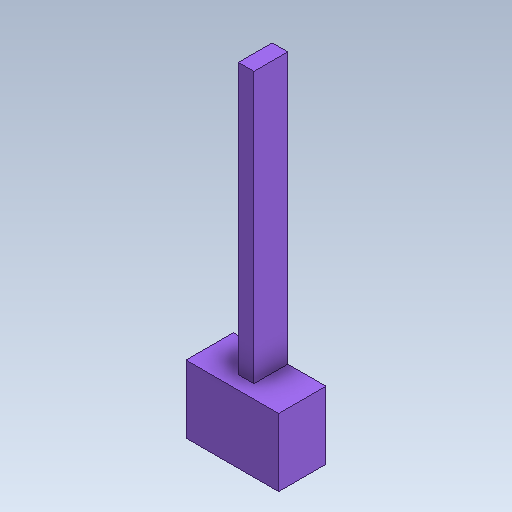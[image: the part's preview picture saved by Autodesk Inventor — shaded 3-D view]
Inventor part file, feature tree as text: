
AUTODESK INVENTOR PART (.ipt)
format: ipt  version: 2020 (Build 240168000, 168)  size: 260,608 bytes
history: native  units: in
note: dims shown in document units (in); Inventor stores cm internally (conversion verified against a paired STEP export)
features: extrude x13, sketch x13, projected_geometry x12
ambient origin geometry x8: Origin, YZ Plane, XZ Plane, XY Plane, X Axis, Y Axis, Z Axis, Center Point
bodies: Solid1 (feature_tree)
feature tree (38):
  extrude  "Extrusion1"  Depth=0.7874in
  extrude  "Extrusion4"  Depth=0.2894in
  extrude  "Extrusion5"  Depth=0.1378in TaperAngle=0.0deg
  extrude  "Extrusion6"  Depth=0.0797in
  extrude  "Extrusion7"  Depth=0.1575in
  extrude  "Extrusion8"  Depth=0.0787in TaperAngle=0.0deg
  extrude  "Extrusion9"  Depth=0.0394in
  extrude  "Extrusion10"  Depth=0.0689in TaperAngle=0.0deg
  extrude  "Extrusion11"  Depth=0.3937in TaperAngle=0.0deg
  extrude  "Extrusion12"  Depth=0.3937in TaperAngle=0.0deg
  extrude  "Extrusion17"  Depth=0.3937in TaperAngle=0.0deg
  extrude  "Extrusion18"  Depth=0.0039in
  extrude  "Extrusion19"  Depth=0.0394in TaperAngle=0.0deg
  sketch  "Sketch1"  dims[d0=0.7874in d1=0.1358in]
  sketch  "Sketch4"  dims[d2=0.1457in d3=0.2894in]
  projected_geometry  "Projected Loop3"
  sketch  "Sketch5"  dims[d4=0.1969in d5=0.1378in d6=0.0in]
  projected_geometry  "Projected Loop4"
  sketch  "Sketch6"  dims[d22=0.0797in d23=0.0797in]
  projected_geometry  "Projected Loop5"
  sketch  "Sketch7"  dims[d24=0.2953in d25=0.1575in]
  projected_geometry  "Projected Loop6"
  sketch  "Sketch8"  dims[d26=0.122in d27=0.0787in d28=0.0in]
  projected_geometry  "Projected Loop7"
  sketch  "Sketch9"  dims[d29=0.0394in d30=0.0394in]
  projected_geometry  "Projected Loop8"
  sketch  "Sketch10"  dims[d31=0.3937in d32=0.0in d33=0.0689in d34=0.0in]
  projected_geometry  "Projected Loop9"
  sketch  "Sketch11"  dims[d35=0.0197in d36=0.3937in d37=0.0in]
  projected_geometry  "Projected Loop10"
  sketch  "Sketch12"  dims[d38=0.0787in d39=0.0in d40=0.3937in d41=0.0in]
  projected_geometry  "Projected Loop11"
  sketch  "Sketch17"  dims[d42=0.3937in d43=0.0in d44=0.3937in d45=0.0in]
  projected_geometry  "Projected Loop16"
  sketch  "Sketch18"  dims[d46=0.3937in d47=0.0in d48=0.0039in]
  projected_geometry  "Projected Loop17"
  sketch  "Sketch19"  dims[d49=0.0039in d50=0.3937in d51=0.0in d63=0.0394in d64=0.0in d65=0.0059in d66=0.0059in d67=0.0394in d68=0.0in d69=0.0059in d70=0.0059in d71=0.0394in d72=0.0in]
  projected_geometry  "Projected Loop18"
